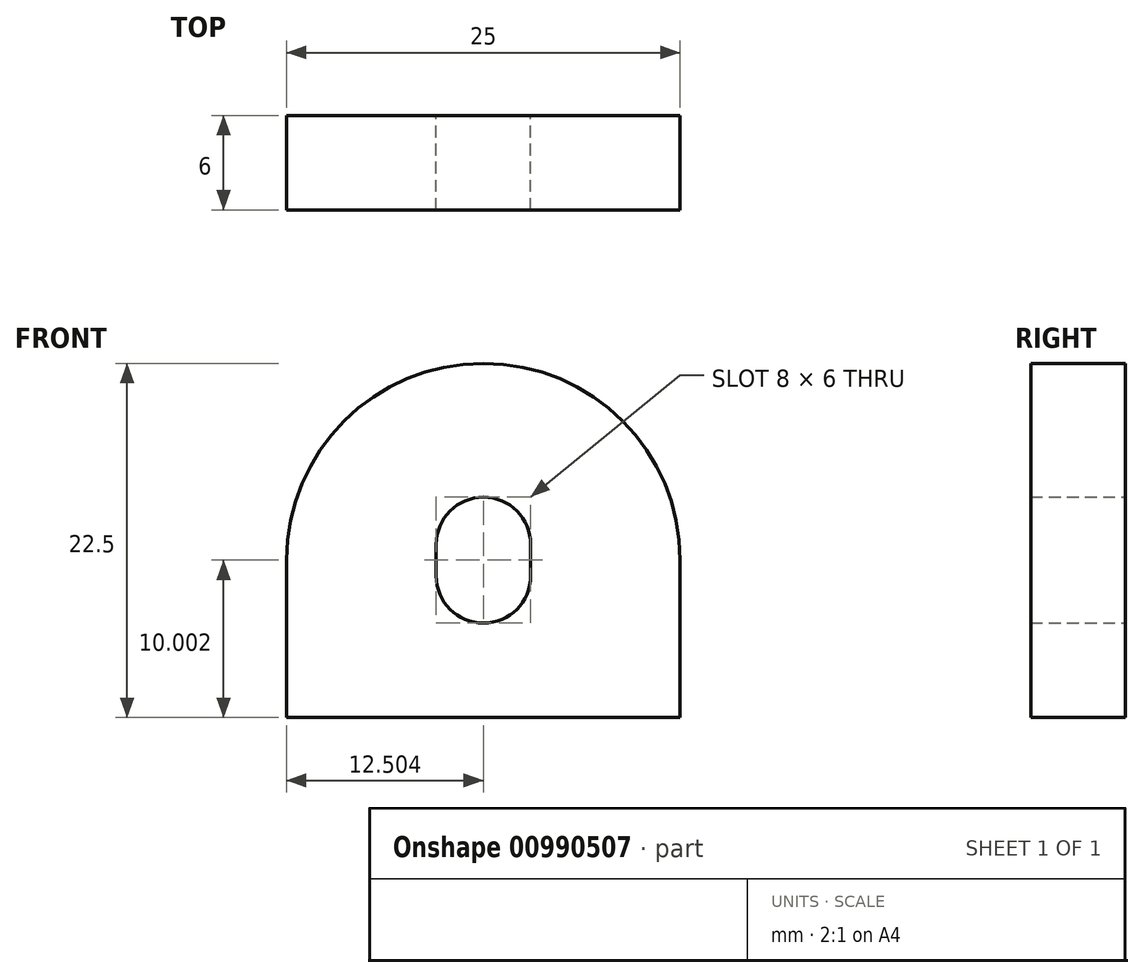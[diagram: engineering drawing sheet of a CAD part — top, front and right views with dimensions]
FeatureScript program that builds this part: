
annotation { "Feature Type Name" : "Feature", "Feature Type Description" : "" }
export const myFeature = defineFeature(function(context is Context, id is Id, definition is map)
    precondition{}
    {
        {
            var Q0;
            Q0=qCreatedBy(makeId("Front.planeOp"),FACE);
            var sketch = newSketch(context, id + "F0", { "sketchPlane" : qUnion([Q0])});
            skLineSegment(sketch, "E0.0.0", {"start": v(-49.75, 10.41) * mm, "end": v(-24.75, 10.41) * mm});
            skLineSegment(sketch, "E0.0.1", {"start": v(-24.75, 10.41) * mm, "end": v(-24.75, 20.41) * mm});
            skArc(sketch, "E0.0.2", {"start": v(-24.75, 20.41) * mm, "mid": v(-37.25, 32.91) * mm, "end": v(-49.75, 20.41) * mm});
            skLineSegment(sketch, "E0.0.3", {"start": v(-49.75, 20.41) * mm, "end": v(-49.75, 10.41) * mm});
            skArc(sketch, "E1.0", {"start": v(-34.25, 21.41) * mm, "mid": v(-37.25, 24.41) * mm, "end": v(-40.25, 21.41) * mm});
            skArc(sketch, "E2.0", {"start": v(-34.25, 19.41) * mm, "mid": v(-37.25, 16.41) * mm, "end": v(-40.25, 19.41) * mm});
            skLineSegment(sketch, "E3.0", {"start": v(-34.25, 19.41) * mm, "end": v(-34.25, 21.41) * mm});
            skLineSegment(sketch, "E4.0", {"start": v(-40.25, 19.41) * mm, "end": v(-40.25, 21.41) * mm});
            skSolve(sketch);
        }
        {
            var Q0;
            Q0=makeQuery(id+"F0.imprint","IMPRINT",FACE,{"disambiguationData":[TD([[makeQuery(id+"F0.imprint","IMPRINT",EDGE,{"derivedFrom":sQuery(id+"F0.wireOp",EDGE,"E0.0.0")}),1.0]])]});
            extrude(context, id + "F1", {"entities" : qUnion([Q0]), "depth" : 6 * mm, "offsetDistance" : 25 * mm});
        }
    });
